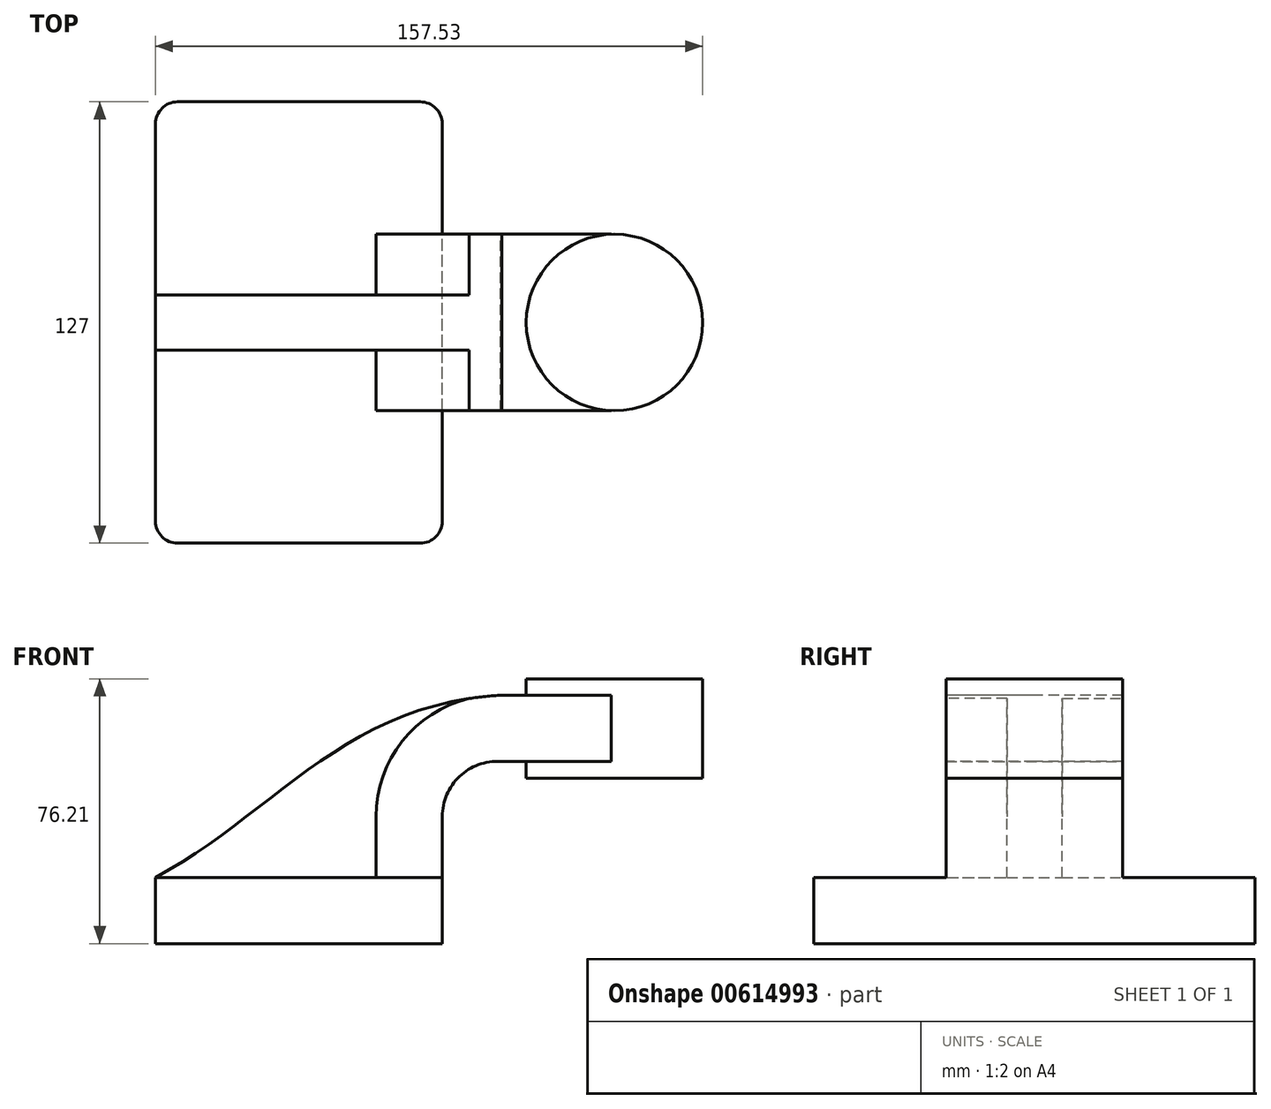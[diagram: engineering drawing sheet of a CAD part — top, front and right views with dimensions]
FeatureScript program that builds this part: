
annotation { "Feature Type Name" : "Feature", "Feature Type Description" : "" }
export const myFeature = defineFeature(function(context is Context, id is Id, definition is map)
    precondition{}
    {
        {
            var Q0;
            Q0=qCreatedBy(makeId("Front.planeOp"),FACE);
            var sketch = newSketch(context, id + "F0", { "sketchPlane" : qUnion([Q0])});
            skLineSegment(sketch, "E0.bottom", {"start": v(-41.28, 9.52) * mm, "end": v(41.27, 9.53) * mm});
            skLineSegment(sketch, "E0.top", {"start": v(-41.28, -9.53) * mm, "end": v(41.28, -9.53) * mm});
            skLineSegment(sketch, "E0.left", {"start": v(-41.28, 9.52) * mm, "end": v(-41.27, -9.53) * mm});
            skLineSegment(sketch, "E0.right", {"start": v(41.28, 9.53) * mm, "end": v(41.28, -9.52) * mm});
            skPoint(sketch, "E0.middle", {"position": v(0, 0) * mm});
            skLineSegment(sketch, "E1.bottom", {"start": v(65.45, 38.1) * mm, "end": v(116.25, 38.1) * mm});
            skLineSegment(sketch, "E1.top", {"start": v(65.45, 66.67) * mm, "end": v(116.25, 66.67) * mm});
            skLineSegment(sketch, "E1.left", {"start": v(65.45, 38.1) * mm, "end": v(65.45, 66.67) * mm});
            skLineSegment(sketch, "E1.right", {"start": v(116.25, 38.1) * mm, "end": v(116.25, 66.67) * mm});
            skPoint(sketch, "E1.middle", {"position": v(90.85, 52.39) * mm});
            skLineSegment(sketch, "E2", {"start": v(41.27, 9.53) * mm, "end": v(41.27, 27.02) * mm});
            skArc(sketch, "E3", {"start": v(58.03, 42.88) * mm, "mid": v(46.24, 38.56) * mm, "end": v(41.28, 27.02) * mm});
            skLineSegment(sketch, "E4", {"start": v(58.03, 42.88) * mm, "end": v(89.93, 42.88) * mm});
            skLineSegment(sketch, "E5.0", {"start": v(22.23, 9.53) * mm, "end": v(22.23, 27.02) * mm});
            skArc(sketch, "E5.1", {"start": v(58.46, 61.93) * mm, "mid": v(32.92, 52.18) * mm, "end": v(22.23, 27.02) * mm});
            skLineSegment(sketch, "E5.2", {"start": v(58.46, 61.93) * mm, "end": v(89.93, 61.93) * mm});
            skLineSegment(sketch, "E6", {"start": v(89.93, 42.88) * mm, "end": v(89.93, 61.93) * mm});
            skFitSpline(sketch, "E7", {"points": [v(-41.28, 9.52) * mm, v(58.46, 61.93) * mm], "startDerivative": vector(99.73, 52.4) * mm, "endDerivative": vector(136.55, 6.71) * mm});
            skLineSegment(sketch, "E8", {"start": v(90.85, 52.39) * mm, "end": v(90.85, 38.1) * mm});
            skLineSegment(sketch, "E9", {"start": v(90.85, 38.1) * mm, "end": v(90.85, 66.67) * mm});
            skSolve(sketch);
        }
        {
            var Q0;
            Q0=makeQuery(id+"F0.imprint","IMPRINT",FACE,{"disambiguationData":[TD([[makeQuery(id+"F0.imprint","IMPRINT",EDGE,{"derivedFrom":sQuery(id+"F0.wireOp",EDGE,"E0.top")}),1.0]])]});
            extrude(context, id + "F1", {"entities" : qUnion([Q0]), "endBound" : BoundingType.SYMMETRIC, "depth" : 127 * mm, "offsetDistance" : 25.4 * mm});
        }
        {
            var Q0;
            {var subQ1=sQuery(id+"F0.wireOp",EDGE,"E2");Q0=makeQuery(id+"F0.imprint","IMPRINT",FACE,{"disambiguationData":[TD([[makeQuery(id+"F0.imprint","IMPRINT",EDGE,{"derivedFrom":subQ1}),1.0]])]});}
            var Q1;
            {var subQ5=sQuery(id+"F0.wireOp",EDGE,"E6");Q1=makeQuery(id+"F0.imprint","IMPRINT",FACE,{"disambiguationData":[TD([[makeQuery(id+"F0.imprint","IMPRINT",EDGE,{"derivedFrom":subQ5}),1.0]])]});}
            extrude(context, id + "F2", {"entities" : qUnion([Q0, Q1]), "operationType" : NewBodyOperationType.ADD, "endBound" : BoundingType.SYMMETRIC, "depth" : 50.8 * mm, "offsetDistance" : 25.4 * mm});
        }
        {
            var Q0;
            {var subQ3=sQuery(id+"F0.wireOp",EDGE,"E5.0");Q0=makeQuery(id+"F0.imprint","IMPRINT",FACE,{"disambiguationData":[TD([[makeQuery(id+"F0.imprint","IMPRINT",EDGE,{"derivedFrom":subQ3}),1.0]])]});}
            extrude(context, id + "F3", {"entities" : qUnion([Q0]), "operationType" : NewBodyOperationType.ADD, "endBound" : BoundingType.SYMMETRIC, "depth" : 15.88 * mm, "offsetDistance" : 25.4 * mm});
        }
        {
            var Q0;
            {var subQ4=sQuery(id+"F0.wireOp",EDGE,"E1.right");Q0=makeQuery(id+"F0.imprint","IMPRINT",FACE,{"disambiguationData":[TD([[makeQuery(id+"F0.imprint","IMPRINT",EDGE,{"derivedFrom":subQ4}),1.0]])]});}
            var Q1;
            Q1=sQuery(id+"F0.wireOp",EDGE,"E9");
            revolve(context, id + "F4", {"operationType" : NewBodyOperationType.ADD, "entities" : qUnion([Q0]), "axis" : qUnion([Q1]), "revolveType" : RevolveType.FULL});
        }
        {
            var Q0;
            Q0=makeQuery(id+"F1.opExtrude","CAP_EDGE",EDGE,{"disambiguationData":[OSD([sQuery(id+"F0.wireOp",EDGE,"E0.right")])],"isStart":false});
            var Q1;
            Q1=makeQuery(id+"F1.opExtrude","CAP_EDGE",EDGE,{"disambiguationData":[OSD([sQuery(id+"F0.wireOp",EDGE,"E0.left")])],"isStart":false});
            var Q2;
            Q2=makeQuery(id+"F1.opExtrude","CAP_EDGE",EDGE,{"disambiguationData":[OSD([sQuery(id+"F0.wireOp",EDGE,"E0.right")])],"isStart":true});
            var Q3;
            Q3=makeQuery(id+"F1.opExtrude","CAP_EDGE",EDGE,{"disambiguationData":[OSD([sQuery(id+"F0.wireOp",EDGE,"E0.left")])],"isStart":true});
            fillet(context, id + "F5", {"entities" : qUnion([Q0, Q1, Q2, Q3]), "radius" : 6.35 * mm, "tangentPropagation" : true, "allowEdgeOverflow" : false});
        }
    });
